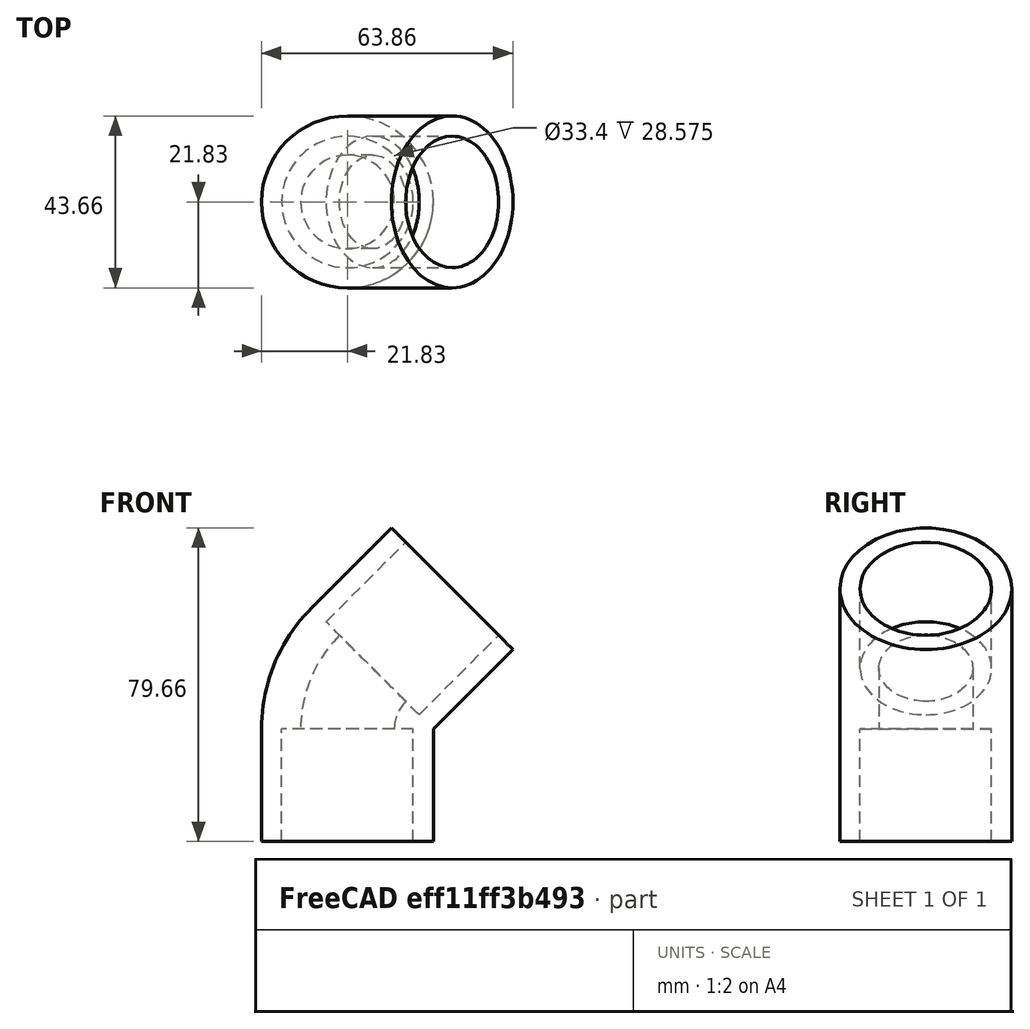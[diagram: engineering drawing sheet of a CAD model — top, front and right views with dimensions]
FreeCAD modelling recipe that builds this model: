
FCSTD DOCUMENT  (FreeCAD 0.17R13303 (Git))
Label: elbow-test
License: All rights reserved
LicenseURL: http://en.wikipedia.org/wiki/All_rights_reserved
objects: Sketcher::SketchObject×4, Part::Cut×3, Part::Sweep×2, Part::Cylinder×2, App::DocumentObjectGroup×1
note: 11 computed .brp shape members not serialized (recipe doc carries the construction recipe); baked Part::Feature solids carry a one-line shape summary decoded from their .brp

FEATURE [Sketcher::SketchObject] BaseSketch
  sketch-geometry (1):
    g0: Circle CenterX=0 CenterY=0 CenterZ=0 NormalX=0 NormalY=0 NormalZ=1 AngleXU=0 Radius=21.8281
FEATURE [Sketcher::SketchObject] PathSketch
  Placement = pos=(0,0,0) rot=(-1,0,0;4.71239rad)
  sketch-geometry (3):
    g0: LineSegment StartX=0 StartY=0 StartZ=0 EndX=0 EndY=-28.575 EndZ=0
    g1: ArcOfCircle CenterX=21.8281 CenterY=0 CenterZ=0 NormalX=0 NormalY=0 NormalZ=1 AngleXU=0 Radius=21.8281 StartAngle=2.35619 EndAngle=3.14159
    g2: LineSegment StartX=6.39331 StartY=15.4348 StartZ=0 EndX=26.5989 EndY=35.6404 EndZ=0
FEATURE [Part::Sweep] Sweep
  Frenet = false
  Sections = -> [BaseSketch]
  Solid = true
  Spine = -> PathSketch [Edge1,Edge2,Edge3]
  Transition = 1
FEATURE [Sketcher::SketchObject] BaseSketch001
  sketch-geometry (1):
    g0: Circle CenterX=0 CenterY=0 CenterZ=0 NormalX=0 NormalY=0 NormalZ=1 AngleXU=0 Radius=11.8872
FEATURE [Sketcher::SketchObject] PathSketch001
  Placement = pos=(0,0,0) rot=(-1,0,0;4.71239rad)
  sketch-geometry (3):
    g0: LineSegment StartX=0 StartY=0 StartZ=0 EndX=0 EndY=-31.4325 EndZ=0
    g1: ArcOfCircle CenterX=21.8281 CenterY=0 CenterZ=0 NormalX=0 NormalY=0 NormalZ=1 AngleXU=0 Radius=21.8281 StartAngle=2.35619 EndAngle=3.14159
    g2: LineSegment StartX=6.39331 StartY=15.4348 StartZ=0 EndX=28.6194 EndY=37.6609 EndZ=0
FEATURE [Part::Sweep] Sweep001
  Frenet = false
  Sections = -> [BaseSketch001]
  Solid = true
  Spine = -> PathSketch001 [Edge1,Edge2,Edge3]
  Transition = 1
FEATURE [Part::Cut] BentCut
  Base = -> Sweep
  Tool = -> Sweep001
FEATURE [Part::Cylinder] InnerCylinder1
  Angle = 360
  AttacherType = Attacher::AttachEngine3D
  Height = 31.4325
  Placement = pos=(0,0,-31.4325) rot=(0,0,1;0rad)
  Radius = 16.7005
FEATURE [Part::Cylinder] InnerCylinder2
  Angle = 360
  AttacherType = Attacher::AttachEngine3D
  Height = 31.4325
  Placement = pos=(6.39331,0,15.4348) rot=(0,1,0;0.785398rad)
  Radius = 16.7005
FEATURE [Part::Cut] PipeCut1
  Base = -> BentCut
  Tool = -> InnerCylinder1
FEATURE [Part::Cut] elbow
  Base = -> PipeCut1
  Tool = -> InnerCylinder2
FEATURE [App::DocumentObjectGroup] elbow_group  label="817-010"
  Group = -> [BaseSketch,PathSketch,Sweep,BaseSketch001,PathSketch001,Sweep001,BentCut,elbow]
